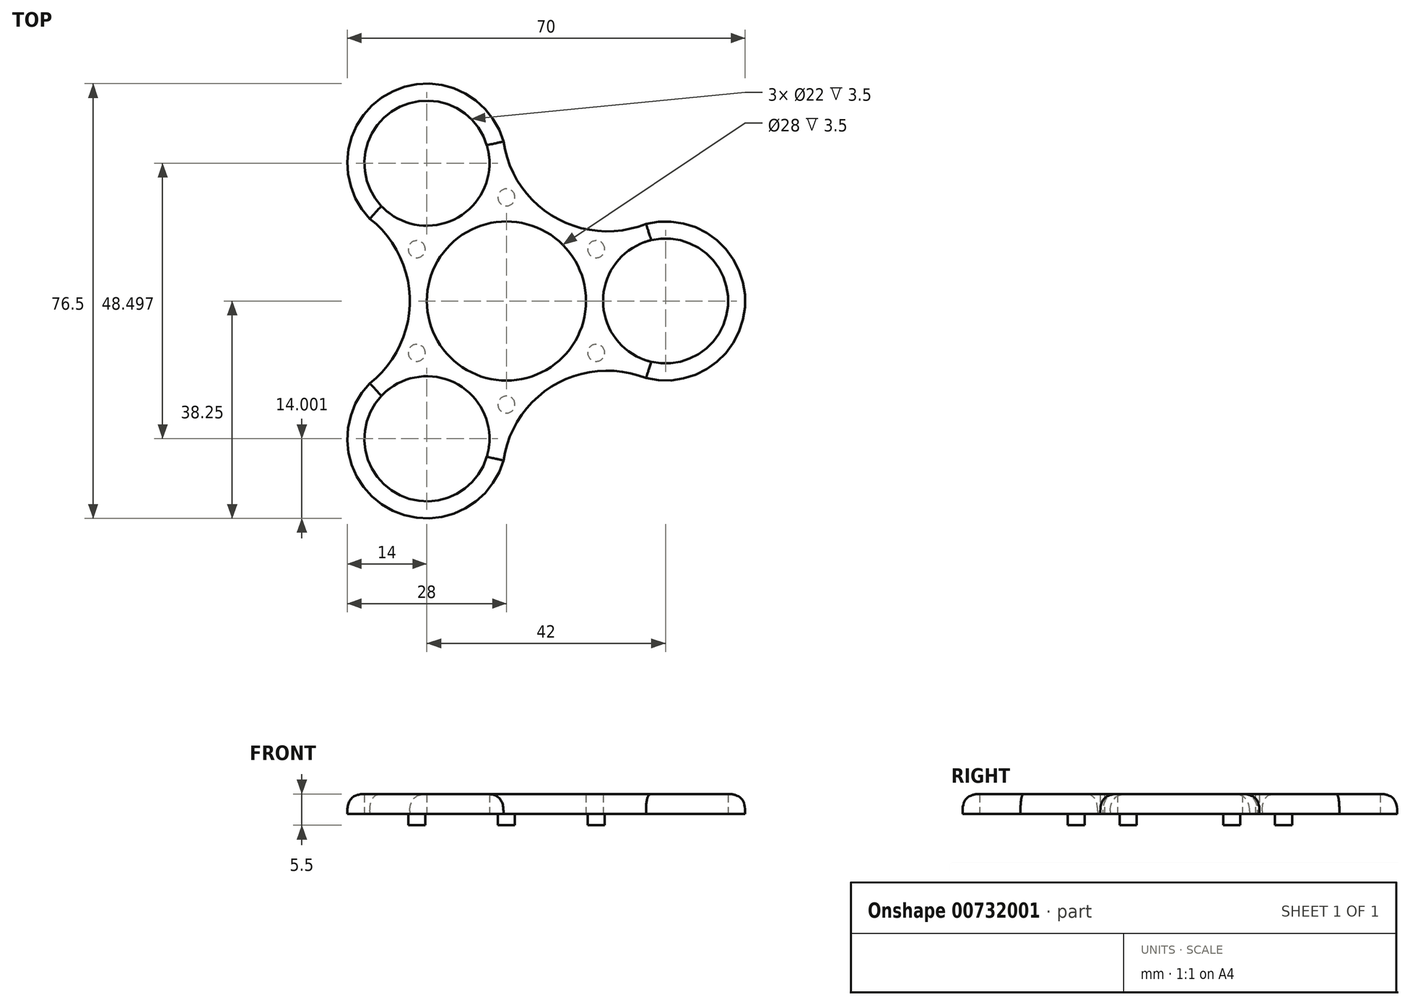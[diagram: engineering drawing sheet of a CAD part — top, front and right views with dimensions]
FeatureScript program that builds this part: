
annotation { "Feature Type Name" : "Feature", "Feature Type Description" : "" }
export const myFeature = defineFeature(function(context is Context, id is Id, definition is map)
    precondition{}
    {
        {
            var Q0;
            Q0=qCreatedBy(makeId("Top.planeOp"),FACE);
            var sketch = newSketch(context, id + "F0", { "sketchPlane" : qUnion([Q0])});
            skCircle(sketch, "E0", {"center": v(0, 0) * mm, "radius": 14 * mm});
            skLineSegment(sketch, "E1", {"start": v(14, 0) * mm, "end": v(17, 0) * mm});
            skLineSegment(sketch, "E2", {"start": v(17, 0) * mm, "end": v(28, 0) * mm});
            skCircle(sketch, "E3", {"center": v(28, 0) * mm, "radius": 11 * mm});
            skArc(sketch, "E4", {"start": v(22.57, -12.9) * mm, "mid": v(42, 0) * mm, "end": v(22.57, 12.9) * mm});
            skArc(sketch, "E5", {"start": v(-24.03, -14.48) * mm, "mid": v(-17, 0) * mm, "end": v(-24.03, 14.48) * mm});
            skArc(sketch, "E6.1.0", {"start": v(24.56, -13.57) * mm, "mid": v(8.5, -14.72) * mm, "end": v(-0.53, -28.05) * mm});
            skArc(sketch, "E6.1.1", {"start": v(-0.1, 26) * mm, "mid": v(-21, 36.37) * mm, "end": v(-22.46, 13.1) * mm});
            skCircle(sketch, "E6.1.2", {"center": v(-14, 24.25) * mm, "radius": 11 * mm});
            skArc(sketch, "E6.2.0", {"start": v(-0.53, 28.05) * mm, "mid": v(8.5, 14.72) * mm, "end": v(24.56, 13.57) * mm});
            skArc(sketch, "E6.2.1", {"start": v(-22.46, -13.1) * mm, "mid": v(-21, -36.37) * mm, "end": v(-0.1, -26) * mm});
            skCircle(sketch, "E6.2.2", {"center": v(-14, -24.25) * mm, "radius": 11 * mm});
            skSolve(sketch);
        }
        {
            var Q0;
            Q0=makeQuery(id+"F0.imprint","IMPRINT",FACE,{"disambiguationData":[TD([[makeQuery(id+"F0.imprint","IMPRINT",EDGE,{"derivedFrom":sQuery(id+"F0.wireOp",EDGE,"E0")}),-1.0]])]});
            extrude(context, id + "F1", {"entities" : qUnion([Q0]), "depth" : 3.5 * mm, "offsetDistance" : 25 * mm});
        }
        {
            var Q0;
            Q0=makeQuery(id+"F1.opExtrude","CAP_EDGE",EDGE,{"disambiguationData":[OSD([sQuery(id+"F0.wireOp",EDGE,"E6.1.0")])],"isStart":false});
            var Q1;
            Q1=makeQuery(id+"F1.opExtrude","CAP_EDGE",EDGE,{"disambiguationData":[OSD([sQuery(id+"F0.wireOp",EDGE,"E5")])],"isStart":false});
            var Q2;
            Q2=makeQuery(id+"F1.opExtrude","CAP_EDGE",EDGE,{"disambiguationData":[OSD([sQuery(id+"F0.wireOp",EDGE,"E6.2.0")])],"isStart":false});
            var Q3;
            Q3=makeQuery(id+"F1.opExtrude","CAP_EDGE",EDGE,{"disambiguationData":[OSD([sQuery(id+"F0.wireOp",EDGE,"E6.2.1")])],"isStart":false});
            var Q4;
            Q4=makeQuery(id+"F1.opExtrude","CAP_EDGE",EDGE,{"disambiguationData":[OSD([sQuery(id+"F0.wireOp",EDGE,"E4")])],"isStart":false});
            var Q5;
            Q5=makeQuery(id+"F1.opExtrude","CAP_EDGE",EDGE,{"disambiguationData":[OSD([sQuery(id+"F0.wireOp",EDGE,"E6.1.1")])],"isStart":false});
            fillet(context, id + "F2", {"entities" : qUnion([Q0, Q1, Q2, Q3, Q4, Q5]), "radius" : 3 * mm, "rho" : 0.5, "crossSection" : FilletCrossSection.CONIC, "allowEdgeOverflow" : false});
        }
        {
            var Q0;
            Q0=qCreatedBy(makeId("Top.planeOp"),FACE);
            var sketch = newSketch(context, id + "F3", { "sketchPlane" : qUnion([Q0])});
            skLineSegment(sketch, "E7.5", {"start": v(0, 18.23) * mm, "end": v(15.79, 9.12) * mm});
            skCircle(sketch, "E8", {"center": v(0, 18.23) * mm, "radius": 1.5 * mm});
            skCircle(sketch, "E9.1.0", {"center": v(-15.79, 9.12) * mm, "radius": 1.5 * mm});
            skLineSegment(sketch, "E9.1.1", {"start": v(-15.79, 9.12) * mm, "end": v(0, 18.23) * mm});
            skCircle(sketch, "E9.2.0", {"center": v(-15.79, -9.12) * mm, "radius": 1.5 * mm});
            skLineSegment(sketch, "E9.2.1", {"start": v(-15.79, -9.12) * mm, "end": v(-15.79, 9.12) * mm});
            skPoint(sketch, "E9.center", {"position": v(0, 0) * mm});
            skCircle(sketch, "E10.1.3.0", {"center": v(0, -18.23) * mm, "radius": 1.5 * mm});
            skLineSegment(sketch, "E10.2.3.0", {"start": v(0, -18.23) * mm, "end": v(-15.79, -9.12) * mm});
            skCircle(sketch, "E10.1.4.0", {"center": v(15.79, -9.12) * mm, "radius": 1.5 * mm});
            skLineSegment(sketch, "E10.2.4.0", {"start": v(15.79, -9.12) * mm, "end": v(0, -18.23) * mm});
            skCircle(sketch, "E10.1.5.0", {"center": v(15.79, 9.12) * mm, "radius": 1.5 * mm});
            skLineSegment(sketch, "E10.2.5.0", {"start": v(15.79, 9.12) * mm, "end": v(15.79, -9.12) * mm});
            skSolve(sketch);
        }
        {
            var Q0;
            {var subQ0=sQuery(id+"F3.wireOp",EDGE,"E9.1.1");var subQ1=sQuery(id+"F3.wireOp",EDGE,"E7.5");var subQ2=makeQuery(id+"F3.imprint","INTERSECT",VERTEX,{"derivedFrom":[subQ1,subQ0]});Q0=makeQuery(id+"F3.imprint","IMPRINT",FACE,{"disambiguationData":[TD([[makeQuery(id+"F3.imprint","IMPRINT",EDGE,{"disambiguationData":[TD([[subQ2,-1.0]])],"derivedFrom":subQ1}),1.0]])]});}
            var Q1;
            {var subQ0=sQuery(id+"F3.wireOp",EDGE,"E9.1.1");var subQ1=sQuery(id+"F3.wireOp",EDGE,"E7.5");var subQ2=makeQuery(id+"F3.imprint","INTERSECT",VERTEX,{"derivedFrom":[subQ1,subQ0]});Q1=makeQuery(id+"F3.imprint","IMPRINT",FACE,{"disambiguationData":[TD([[makeQuery(id+"F3.imprint","IMPRINT",EDGE,{"disambiguationData":[TD([[subQ2,-1.0]])],"derivedFrom":subQ1}),-1.0]])]});}
            var Q2;
            {var subQ0=sQuery(id+"F3.wireOp",EDGE,"E9.1.1");var subQ1=sQuery(id+"F3.wireOp",EDGE,"E9.1.0");var subQ2=makeQuery(id+"F3.imprint","INTERSECT",VERTEX,{"derivedFrom":[subQ1,subQ0]});Q2=makeQuery(id+"F3.imprint","IMPRINT",FACE,{"disambiguationData":[TD([[makeQuery(id+"F3.imprint","IMPRINT",EDGE,{"disambiguationData":[TD([[subQ2,-1.0]])],"derivedFrom":subQ1}),1.0]])]});}
            var Q3;
            {var subQ0=sQuery(id+"F3.wireOp",EDGE,"E9.1.1");var subQ1=sQuery(id+"F3.wireOp",EDGE,"E9.1.0");var subQ2=makeQuery(id+"F3.imprint","INTERSECT",VERTEX,{"derivedFrom":[subQ1,subQ0]});Q3=makeQuery(id+"F3.imprint","IMPRINT",FACE,{"disambiguationData":[TD([[makeQuery(id+"F3.imprint","IMPRINT",EDGE,{"disambiguationData":[TD([[subQ2,1.0]])],"derivedFrom":subQ1}),1.0]])]});}
            var Q4;
            {var subQ0=sQuery(id+"F3.wireOp",EDGE,"E10.2.5.0");var subQ1=sQuery(id+"F3.wireOp",EDGE,"E7.5");var subQ2=makeQuery(id+"F3.imprint","INTERSECT",VERTEX,{"derivedFrom":[subQ1,subQ0]});Q4=makeQuery(id+"F3.imprint","IMPRINT",FACE,{"disambiguationData":[TD([[makeQuery(id+"F3.imprint","IMPRINT",EDGE,{"disambiguationData":[TD([[subQ2,1.0]])],"derivedFrom":subQ1}),1.0]])]});}
            var Q5;
            {var subQ0=sQuery(id+"F3.wireOp",EDGE,"E10.2.5.0");var subQ1=sQuery(id+"F3.wireOp",EDGE,"E7.5");var subQ2=makeQuery(id+"F3.imprint","INTERSECT",VERTEX,{"derivedFrom":[subQ1,subQ0]});Q5=makeQuery(id+"F3.imprint","IMPRINT",FACE,{"disambiguationData":[TD([[makeQuery(id+"F3.imprint","IMPRINT",EDGE,{"disambiguationData":[TD([[subQ2,1.0]])],"derivedFrom":subQ1}),-1.0]])]});}
            var Q6;
            {var subQ0=sQuery(id+"F3.wireOp",EDGE,"E10.2.3.0");var subQ1=sQuery(id+"F3.wireOp",EDGE,"E10.1.3.0");var subQ2=makeQuery(id+"F3.imprint","INTERSECT",VERTEX,{"derivedFrom":[subQ1,subQ0]});Q6=makeQuery(id+"F3.imprint","IMPRINT",FACE,{"disambiguationData":[TD([[makeQuery(id+"F3.imprint","IMPRINT",EDGE,{"disambiguationData":[TD([[subQ2,-1.0]])],"derivedFrom":subQ1}),1.0]])]});}
            var Q7;
            {var subQ0=sQuery(id+"F3.wireOp",EDGE,"E10.2.3.0");var subQ1=sQuery(id+"F3.wireOp",EDGE,"E10.1.3.0");var subQ2=makeQuery(id+"F3.imprint","INTERSECT",VERTEX,{"derivedFrom":[subQ1,subQ0]});Q7=makeQuery(id+"F3.imprint","IMPRINT",FACE,{"disambiguationData":[TD([[makeQuery(id+"F3.imprint","IMPRINT",EDGE,{"disambiguationData":[TD([[subQ2,1.0]])],"derivedFrom":subQ1}),1.0]])]});}
            var Q8;
            {var subQ0=sQuery(id+"F3.wireOp",EDGE,"E9.2.1");var subQ1=sQuery(id+"F3.wireOp",EDGE,"E9.2.0");var subQ2=makeQuery(id+"F3.imprint","INTERSECT",VERTEX,{"derivedFrom":[subQ1,subQ0]});Q8=makeQuery(id+"F3.imprint","IMPRINT",FACE,{"disambiguationData":[TD([[makeQuery(id+"F3.imprint","IMPRINT",EDGE,{"disambiguationData":[TD([[subQ2,1.0]])],"derivedFrom":subQ1}),1.0]])]});}
            var Q9;
            {var subQ0=sQuery(id+"F3.wireOp",EDGE,"E9.2.1");var subQ1=sQuery(id+"F3.wireOp",EDGE,"E9.2.0");var subQ2=makeQuery(id+"F3.imprint","INTERSECT",VERTEX,{"derivedFrom":[subQ1,subQ0]});Q9=makeQuery(id+"F3.imprint","IMPRINT",FACE,{"disambiguationData":[TD([[makeQuery(id+"F3.imprint","IMPRINT",EDGE,{"disambiguationData":[TD([[subQ2,-1.0]])],"derivedFrom":subQ1}),1.0]])]});}
            var Q10;
            {var subQ0=sQuery(id+"F3.wireOp",EDGE,"E10.2.4.0");var subQ1=sQuery(id+"F3.wireOp",EDGE,"E10.1.4.0");var subQ2=makeQuery(id+"F3.imprint","INTERSECT",VERTEX,{"derivedFrom":[subQ1,subQ0]});Q10=makeQuery(id+"F3.imprint","IMPRINT",FACE,{"disambiguationData":[TD([[makeQuery(id+"F3.imprint","IMPRINT",EDGE,{"disambiguationData":[TD([[subQ2,1.0]])],"derivedFrom":subQ1}),1.0]])]});}
            var Q11;
            {var subQ0=sQuery(id+"F3.wireOp",EDGE,"E10.2.4.0");var subQ1=sQuery(id+"F3.wireOp",EDGE,"E10.1.4.0");var subQ2=makeQuery(id+"F3.imprint","INTERSECT",VERTEX,{"derivedFrom":[subQ1,subQ0]});Q11=makeQuery(id+"F3.imprint","IMPRINT",FACE,{"disambiguationData":[TD([[makeQuery(id+"F3.imprint","IMPRINT",EDGE,{"disambiguationData":[TD([[subQ2,-1.0]])],"derivedFrom":subQ1}),1.0]])]});}
            extrude(context, id + "F4", {"entities" : qUnion([Q0, Q1, Q2, Q3, Q4, Q5, Q6, Q7, Q8, Q9, Q10, Q11]), "operationType" : NewBodyOperationType.ADD, "oppositeDirection" : true, "depth" : 2 * mm, "offsetDistance" : 25 * mm});
        }
    });
